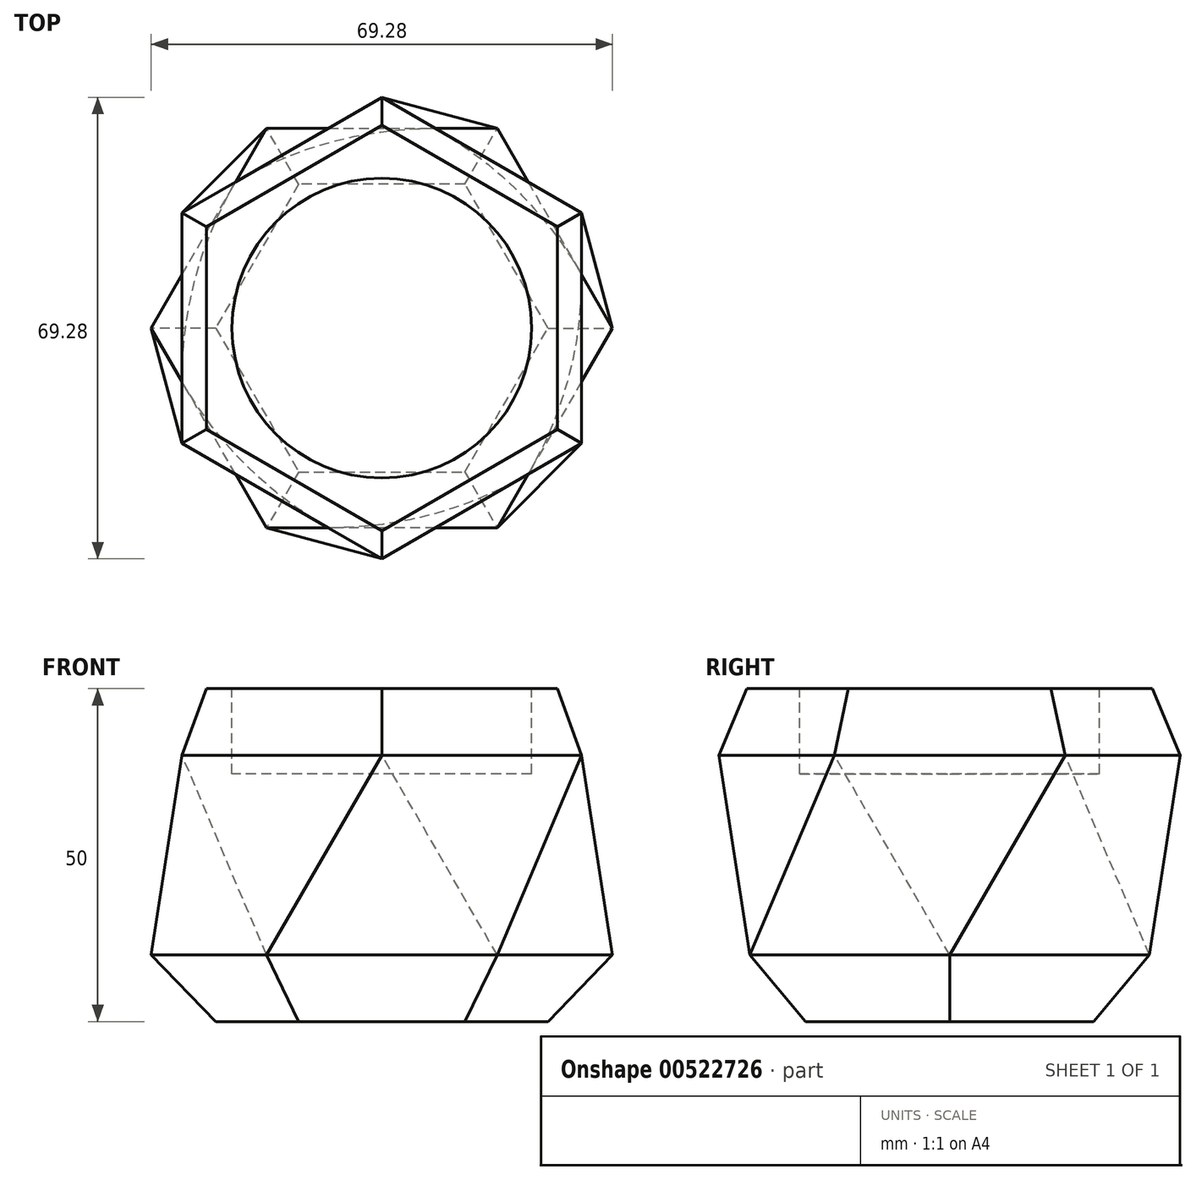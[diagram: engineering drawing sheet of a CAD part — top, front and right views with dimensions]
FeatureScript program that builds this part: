
annotation { "Feature Type Name" : "Feature", "Feature Type Description" : "" }
export const myFeature = defineFeature(function(context is Context, id is Id, definition is map)
    precondition{}
    {
        {
            var Q0;
            Q0=qCreatedBy(makeId("Top.planeOp"),FACE);
            var sketch = newSketch(context, id + "F0", { "sketchPlane" : qUnion([Q0])});
            skCircle(sketch, "E0.cCircle", {"center": v(0, 0) * mm, "radius": 30 * mm, "construction": true});
            skLineSegment(sketch, "E0.0", {"start": v(17.32, 30) * mm, "end": v(34.64, 0) * mm});
            skLineSegment(sketch, "E0.1", {"start": v(34.64, 0) * mm, "end": v(17.32, -30) * mm});
            skLineSegment(sketch, "E0.2", {"start": v(17.32, -30) * mm, "end": v(-17.32, -30) * mm});
            skLineSegment(sketch, "E0.3", {"start": v(-17.32, -30) * mm, "end": v(-34.64, 0) * mm});
            skLineSegment(sketch, "E0.4", {"start": v(-34.64, 0) * mm, "end": v(-17.32, 30) * mm});
            skLineSegment(sketch, "E0.5", {"start": v(-17.32, 30) * mm, "end": v(17.32, 30) * mm});
            skPoint(sketch, "E0.0.midPoint", {"position": v(25.98, 15) * mm});
            skSolve(sketch);
        }
        {
            var Q0;
            Q0=qCreatedBy(makeId("Top.planeOp"),FACE);
            cPlane(context, id + "F1", {"entities" : qUnion([Q0]), "cplaneType" : CPlaneType.OFFSET, "offset" : 30 * mm, "width" : 150 * mm, "height" : 150 * mm});
        }
        {
            var Q0;
            Q0=qCreatedBy(id+"F1.planeOp",FACE);
            var sketch = newSketch(context, id + "F2", { "sketchPlane" : qUnion([Q0])});
            skCircle(sketch, "E1.cCircle", {"center": v(0, 0) * mm, "radius": 30 * mm, "construction": true});
            skLineSegment(sketch, "E1.0", {"start": v(-30, 17.32) * mm, "end": v(0, 34.64) * mm});
            skLineSegment(sketch, "E1.1", {"start": v(0, 34.64) * mm, "end": v(30, 17.32) * mm});
            skLineSegment(sketch, "E1.2", {"start": v(30, 17.32) * mm, "end": v(30, -17.32) * mm});
            skLineSegment(sketch, "E1.3", {"start": v(30, -17.32) * mm, "end": v(0, -34.64) * mm});
            skLineSegment(sketch, "E1.4", {"start": v(0, -34.64) * mm, "end": v(-30, -17.32) * mm});
            skLineSegment(sketch, "E1.5", {"start": v(-30, -17.32) * mm, "end": v(-30, 17.32) * mm});
            skPoint(sketch, "E1.0.midPoint", {"position": v(-15, 25.98) * mm});
            skSolve(sketch);
        }
        {
            var Q0;
            Q0=makeQuery(id+"F0.imprint","IMPRINT",FACE,{"disambiguationData":[TD([[makeQuery(id+"F0.imprint","IMPRINT",EDGE,{"derivedFrom":sQuery(id+"F0.wireOp",EDGE,"E0.0")}),-1.0]])]});
            var Q1;
            Q1=makeQuery(id+"F2.imprint","IMPRINT",FACE,{"disambiguationData":[TD([[makeQuery(id+"F2.imprint","IMPRINT",EDGE,{"derivedFrom":sQuery(id+"F2.wireOp",EDGE,"E1.0")}),-1.0]])]});
            loft(context, id + "F3", {"sheetProfilesArray" : [{ "sheetProfileEntities" : qUnion([Q0]) }, { "sheetProfileEntities" : qUnion([Q1]) }]});
        }
        {
            var Q0;
            Q0=makeQuery(id+"F3.opLoft","CAP_FACE",FACE,{"disambiguationData":[OSD([makeQuery(id+"F0.imprint","IMPRINT",FACE,{"disambiguationData":[TD([[makeQuery(id+"F0.imprint","IMPRINT",EDGE,{"derivedFrom":sQuery(id+"F0.wireOp",EDGE,"E0.0")}),-1.0]])]})])],"isStart":true});
            extrude(context, id + "F4", {"entities" : qUnion([Q0]), "operationType" : NewBodyOperationType.ADD, "depth" : 10 * mm, "offsetDistance" : 25 * mm, "hasDraft" : true, "draftAngle" : 40 * degree, "draftPullDirection" : true});
        }
        {
            var Q0;
            Q0=makeQuery(id+"F3.opLoft","CAP_FACE",FACE,{"disambiguationData":[OSD([makeQuery(id+"F2.imprint","IMPRINT",FACE,{"disambiguationData":[TD([[makeQuery(id+"F2.imprint","IMPRINT",EDGE,{"derivedFrom":sQuery(id+"F2.wireOp",EDGE,"E1.0")}),-1.0]])]})])],"isStart":true});
            extrude(context, id + "F5", {"entities" : qUnion([Q0]), "operationType" : NewBodyOperationType.ADD, "depth" : 10 * mm, "offsetDistance" : 25 * mm, "hasDraft" : true, "draftAngle" : 20 * degree, "draftPullDirection" : true});
        }
        {
            var Q0;
            Q0=makeQuery(id+"F5.opExtrude","CAP_FACE",FACE,{"disambiguationData":[OSD([makeQuery(id+"F2.imprint","IMPRINT",FACE,{"disambiguationData":[TD([[makeQuery(id+"F2.imprint","IMPRINT",EDGE,{"derivedFrom":sQuery(id+"F2.wireOp",EDGE,"E1.0")}),-1.0]])]})])],"isStart":false});
            var sketch = newSketch(context, id + "F6", { "sketchPlane" : qUnion([Q0])});
            skCircle(sketch, "E2", {"center": v(0, 0) * mm, "radius": 22.5 * mm});
            skSolve(sketch);
        }
        {
            var Q0;
            Q0=makeQuery(id+"F6.imprint","IMPRINT",FACE,{"disambiguationData":[TD([[makeQuery(id+"F6.imprint","IMPRINT",EDGE,{"derivedFrom":sQuery(id+"F6.wireOp",EDGE,"E2")}),1.0]])]});
            extrude(context, id + "F7", {"entities" : qUnion([Q0]), "operationType" : NewBodyOperationType.REMOVE, "oppositeDirection" : true, "depth" : 12.8 * mm, "offsetDistance" : 25 * mm});
        }
    });
